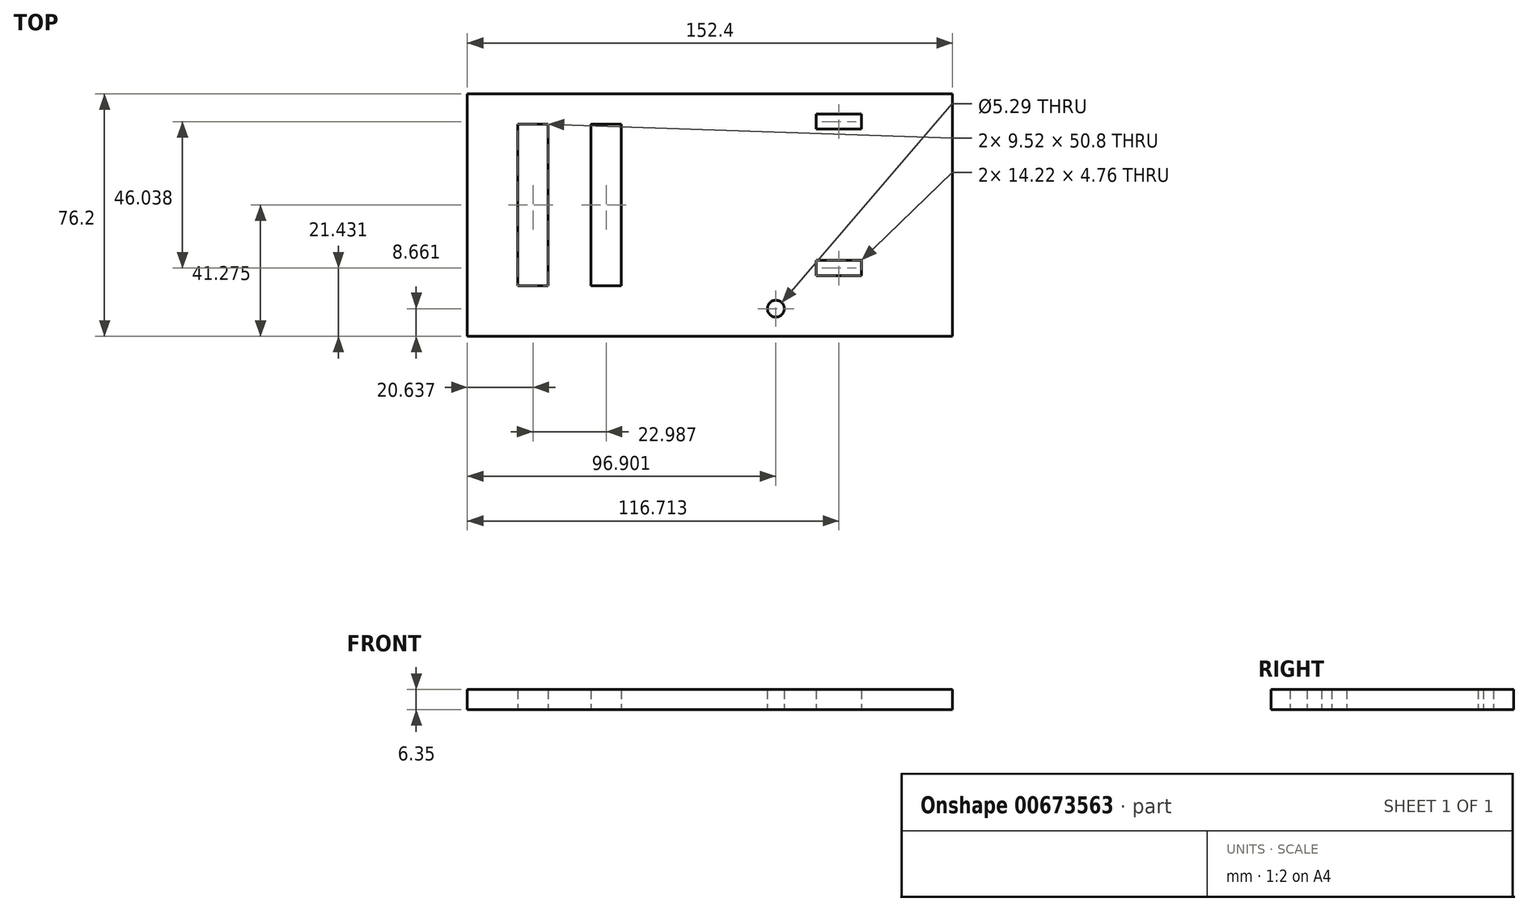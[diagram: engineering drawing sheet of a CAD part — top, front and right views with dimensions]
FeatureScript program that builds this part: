
annotation { "Feature Type Name" : "Feature", "Feature Type Description" : "" }
export const myFeature = defineFeature(function(context is Context, id is Id, definition is map)
    precondition{}
    {
        {
            var Q0;
            Q0=qCreatedBy(makeId("Top.planeOp"),FACE);
            var sketch = newSketch(context, id + "F0", { "sketchPlane" : qUnion([Q0])});
            skLineSegment(sketch, "E0.bottom", {"start": v(0, 0) * mm, "end": v(152.4, 0) * mm});
            skLineSegment(sketch, "E0.top", {"start": v(0, -76.2) * mm, "end": v(152.4, -76.2) * mm});
            skLineSegment(sketch, "E0.left", {"start": v(0, 0) * mm, "end": v(0, -76.2) * mm});
            skLineSegment(sketch, "E0.right", {"start": v(152.4, 0) * mm, "end": v(152.4, -76.2) * mm});
            skLineSegment(sketch, "E1.bottom", {"start": v(15.88, -9.52) * mm, "end": v(25.4, -9.52) * mm});
            skLineSegment(sketch, "E1.top", {"start": v(15.88, -60.33) * mm, "end": v(25.4, -60.33) * mm});
            skLineSegment(sketch, "E1.left", {"start": v(15.88, -9.52) * mm, "end": v(15.88, -60.33) * mm});
            skLineSegment(sketch, "E1.right", {"start": v(25.4, -9.52) * mm, "end": v(25.4, -60.33) * mm});
            skLineSegment(sketch, "E2.bottom", {"start": v(38.86, -60.33) * mm, "end": v(48.39, -60.33) * mm});
            skLineSegment(sketch, "E2.top", {"start": v(38.86, -9.52) * mm, "end": v(48.39, -9.52) * mm});
            skLineSegment(sketch, "E2.left", {"start": v(38.86, -60.32) * mm, "end": v(38.86, -9.52) * mm});
            skLineSegment(sketch, "E2.right", {"start": v(48.39, -60.32) * mm, "end": v(48.39, -9.52) * mm});
            skLineSegment(sketch, "E3.bottom", {"start": v(109.6, -6.35) * mm, "end": v(123.83, -6.35) * mm});
            skLineSegment(sketch, "E3.top", {"start": v(109.6, -11.11) * mm, "end": v(123.83, -11.11) * mm});
            skLineSegment(sketch, "E3.left", {"start": v(109.6, -6.35) * mm, "end": v(109.6, -11.11) * mm});
            skLineSegment(sketch, "E3.right", {"start": v(123.83, -6.35) * mm, "end": v(123.83, -11.11) * mm});
            skLineSegment(sketch, "E4.bottom", {"start": v(109.6, -52.39) * mm, "end": v(123.83, -52.39) * mm});
            skLineSegment(sketch, "E4.top", {"start": v(109.6, -57.15) * mm, "end": v(123.83, -57.15) * mm});
            skLineSegment(sketch, "E4.left", {"start": v(109.6, -52.39) * mm, "end": v(109.6, -57.15) * mm});
            skLineSegment(sketch, "E4.right", {"start": v(123.83, -52.39) * mm, "end": v(123.83, -57.15) * mm});
            skCircle(sketch, "E5", {"center": v(96.9, -67.54) * mm, "radius": 2.65 * mm});
            skSolve(sketch);
        }
        {
            var Q0;
            Q0=makeQuery(id+"F0.imprint","IMPRINT",FACE,{"disambiguationData":[TD([[makeQuery(id+"F0.imprint","IMPRINT",EDGE,{"derivedFrom":sQuery(id+"F0.wireOp",EDGE,"E0.bottom")}),-1.0]])]});
            extrude(context, id + "F1", {"entities" : qUnion([Q0]), "depth" : 6.35 * mm, "offsetDistance" : 25.4 * mm});
        }
    });
